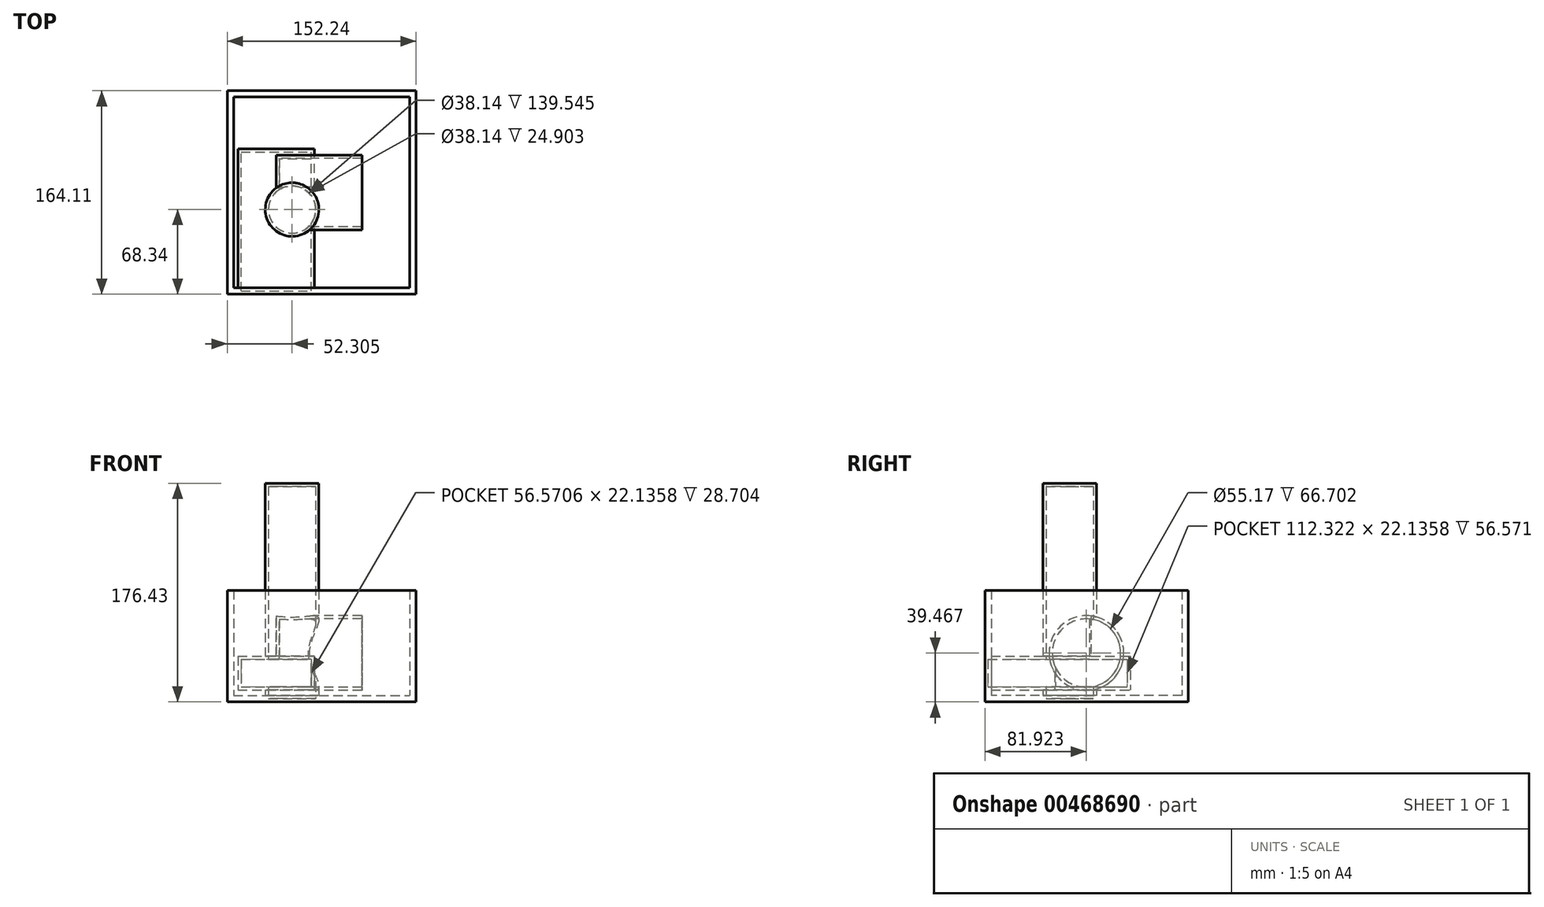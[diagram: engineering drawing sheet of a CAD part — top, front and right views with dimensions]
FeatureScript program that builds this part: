
annotation { "Feature Type Name" : "Feature", "Feature Type Description" : "" }
export const myFeature = defineFeature(function(context is Context, id is Id, definition is map)
    precondition{}
    {
        {
            var Q0;
            Q0=qCreatedBy(makeId("Top.planeOp"),FACE);
            var sketch = newSketch(context, id + "F0", { "sketchPlane" : qUnion([Q0])});
            skLineSegment(sketch, "E0.bottom", {"start": v(-39.42, 46.7) * mm, "end": v(112.82, 46.7) * mm});
            skLineSegment(sketch, "E0.top", {"start": v(-39.42, -117.4) * mm, "end": v(112.82, -117.4) * mm});
            skLineSegment(sketch, "E0.left", {"start": v(-39.42, 46.7) * mm, "end": v(-39.42, -117.4) * mm});
            skLineSegment(sketch, "E0.right", {"start": v(112.82, 46.7) * mm, "end": v(112.82, -117.4) * mm});
            skPoint(sketch, "E0.middle", {"position": v(36.7, -35.35) * mm});
            skSolve(sketch);
        }
        {
            var Q0;
            Q0=makeQuery(id+"F0.imprint","IMPRINT",FACE,{"disambiguationData":[TD([[makeQuery(id+"F0.imprint","IMPRINT",EDGE,{"derivedFrom":sQuery(id+"F0.wireOp",EDGE,"E0.bottom")}),-1.0]])]});
            extrude(context, id + "F1", {"entities" : qUnion([Q0]), "depth" : 90.08 * mm});
        }
        {
            var Q0;
            Q0=makeQuery(id+"F1.opExtrude","CAP_FACE",FACE,{"disambiguationData":[OSD([sQuery(id+"F0.wireOp",EDGE,"E0.bottom"),sQuery(id+"F0.wireOp",EDGE,"E0.top"),sQuery(id+"F0.wireOp",EDGE,"E0.left"),sQuery(id+"F0.wireOp",EDGE,"E0.right")])],"isStart":false});
            shell(context, id + "F2", {"entities" : qUnion([Q0]), "thickness" : 5.08 * mm});
        }
        {
            var Q0;
            Q0=makeQuery(id+"F2.opShell","OFFSET_FACE",FACE,{"disambiguationData":[OSD([sQuery(id+"F0.wireOp",EDGE,"E0.bottom"),sQuery(id+"F0.wireOp",EDGE,"E0.top"),sQuery(id+"F0.wireOp",EDGE,"E0.left"),sQuery(id+"F0.wireOp",EDGE,"E0.right")])]});
            var sketch = newSketch(context, id + "F3", { "sketchPlane" : qUnion([Q0])});
            skCircle(sketch, "E1", {"center": v(12.89, -49.06) * mm, "radius": 21.6 * mm});
            skSolve(sketch);
        }
        {
            var Q0;
            Q0 = qSketchRegion(id + "F3", true);
            extrude(context, id + "F4", {"entities" : qUnion([Q0]), "operationType" : NewBodyOperationType.ADD, "depth" : 171.35 * mm});
        }
        {
            var Q0;
            Q0=qCreatedBy(makeId("Front.planeOp"),FACE);
            var sketch = newSketch(context, id + "F5", { "sketchPlane" : qUnion([Q0])});
            skLineSegment(sketch, "E2.bottom", {"start": v(-30.83, 36.88) * mm, "end": v(30.83, 36.88) * mm});
            skLineSegment(sketch, "E2.top", {"start": v(-30.83, 9.67) * mm, "end": v(30.83, 9.67) * mm});
            skLineSegment(sketch, "E2.left", {"start": v(-30.83, 36.88) * mm, "end": v(-30.83, 9.67) * mm});
            skLineSegment(sketch, "E2.right", {"start": v(30.83, 36.88) * mm, "end": v(30.83, 9.67) * mm});
            skPoint(sketch, "E2.middle", {"position": v(0, 23.28) * mm});
            skSolve(sketch);
        }
        {
            var Q0;
            Q0 = qSketchRegion(id + "F5", true);
            extrude(context, id + "F6", {"entities" : qUnion([Q0]), "depth" : 114.63 * mm, "offsetDistance" : 25.4 * mm});
        }
        {
            var Q0;
            Q0=qCreatedBy(makeId("Right.planeOp"),FACE);
            var sketch = newSketch(context, id + "F7", { "sketchPlane" : qUnion([Q0])});
            skCircle(sketch, "E3", {"center": v(-35.48, 39.47) * mm, "radius": 30.13 * mm});
            skSolve(sketch);
        }
        {
            var Q0;
            Q0=makeQuery(id+"F7.imprint","IMPRINT",FACE,{"disambiguationData":[TD([[makeQuery(id+"F7.imprint","IMPRINT",EDGE,{"derivedFrom":sQuery(id+"F7.wireOp",EDGE,"E3")}),1.0]])]});
            extrude(context, id + "F8", {"entities" : qUnion([Q0]), "operationType" : NewBodyOperationType.ADD, "depth" : 69.24 * mm, "offsetDistance" : 25.4 * mm});
        }
        {
            var Q0;
            Q0=makeQuery(id+"F8.opExtrude","CAP_FACE",FACE,{"disambiguationData":[OSD([sQuery(id+"F7.wireOp",EDGE,"E3")])],"isStart":false});
            shell(context, id + "F9", {"entities" : qUnion([Q0]), "thickness" : 2.54 * mm});
        }
        {
            var Q0;
            Q0=qCreatedBy(makeId("Right.planeOp"),FACE);
            var sketch = newSketch(context, id + "F10", { "sketchPlane" : qUnion([Q0])});
            skLineSegment(sketch, "E4.bottom", {"start": v(52.59, 33.2) * mm, "end": v(52.18, 33.2) * mm});
            skLineSegment(sketch, "E4.top", {"start": v(52.59, 0) * mm, "end": v(52.18, 0) * mm});
            skLineSegment(sketch, "E4.left", {"start": v(52.59, 33.2) * mm, "end": v(52.59, 0) * mm});
            skLineSegment(sketch, "E4.right", {"start": v(52.18, 33.2) * mm, "end": v(52.18, 0) * mm});
            skLineSegment(sketch, "E5.bottom", {"start": v(79.38, 0) * mm, "end": v(83.54, 0) * mm});
            skLineSegment(sketch, "E5.top", {"start": v(79.38, 30.97) * mm, "end": v(83.54, 30.97) * mm});
            skLineSegment(sketch, "E5.left", {"start": v(79.38, 0) * mm, "end": v(79.38, 30.97) * mm});
            skLineSegment(sketch, "E5.right", {"start": v(83.54, 0) * mm, "end": v(83.54, 30.97) * mm});
            skLineSegment(sketch, "E6.bottom", {"start": v(92.9, 98.8) * mm, "end": v(113.46, 98.8) * mm});
            skLineSegment(sketch, "E6.top", {"start": v(92.9, 78.97) * mm, "end": v(113.46, 78.97) * mm});
            skLineSegment(sketch, "E6.left", {"start": v(92.9, 98.8) * mm, "end": v(92.9, 78.97) * mm});
            skLineSegment(sketch, "E6.right", {"start": v(113.46, 98.8) * mm, "end": v(113.46, 78.97) * mm});
            skSolve(sketch);
        }
        {
            var Q0;
            Q0=sQuery(id+"F10.wireOp",EDGE,"E6.right");
            var Q1;
            Q1=sQuery(id+"F10.wireOp",EDGE,"E6.left");
            var Q2;
            Q2=sQuery(id+"F10.wireOp",EDGE,"E6.bottom");
            var Q3;
            Q3=sQuery(id+"F10.wireOp",EDGE,"E6.top");
            extrude(context, id + "F11", {"bodyType" : ToolBodyType.SURFACE, "surfaceEntities" : qUnion([Q0, Q1, Q2, Q3]), "depth" : 74.64 * mm, "offsetDistance" : 25.4 * mm});
        }
    });
